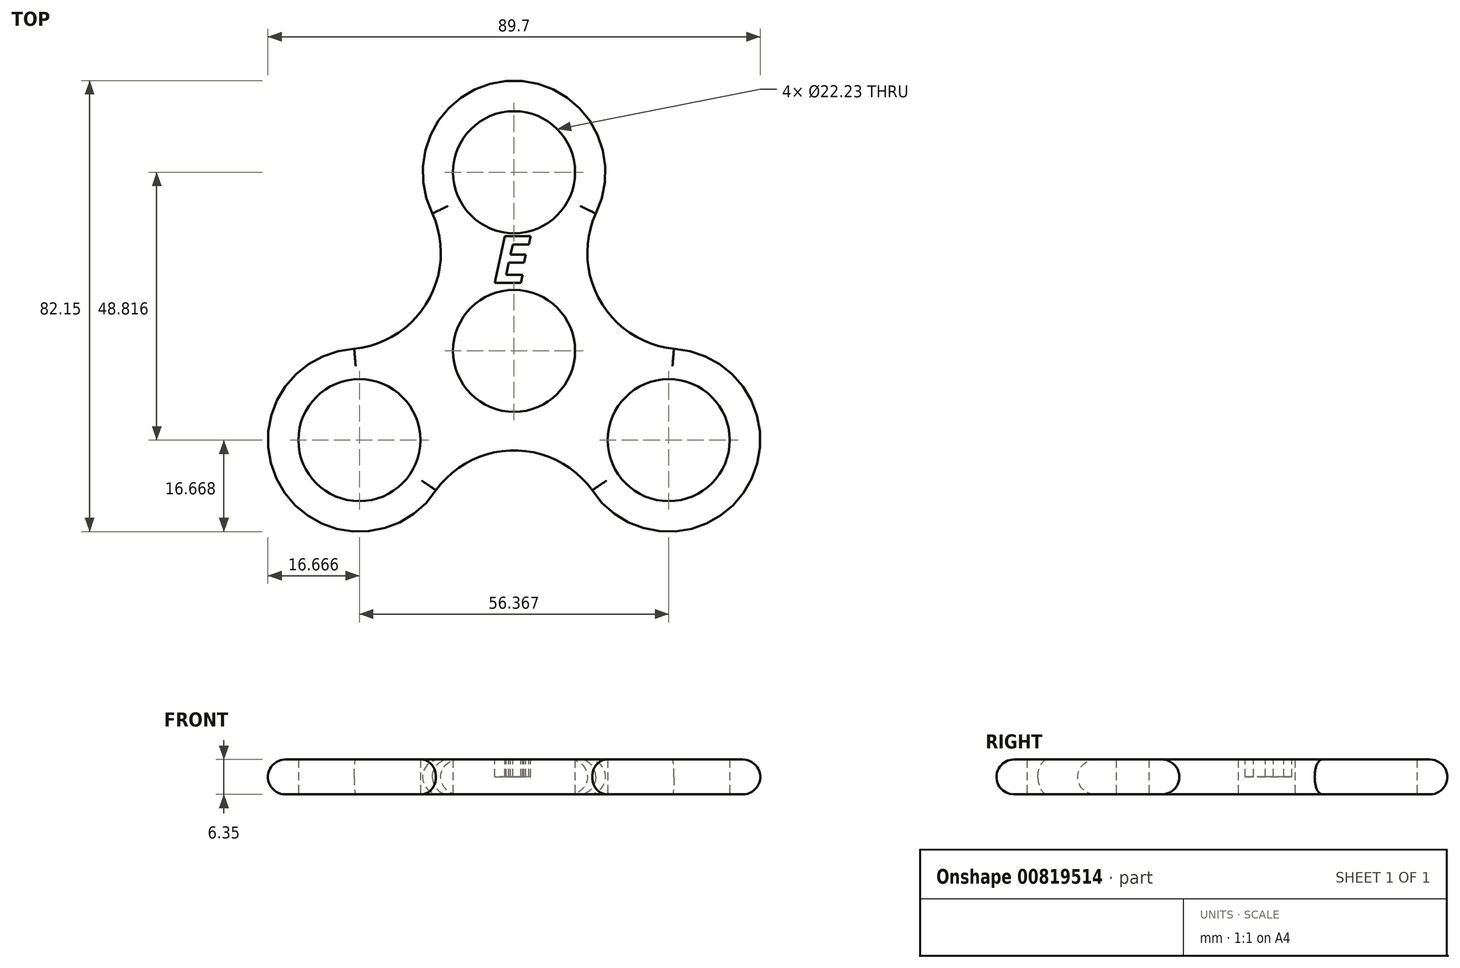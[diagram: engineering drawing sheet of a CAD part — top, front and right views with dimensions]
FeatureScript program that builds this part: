
annotation { "Feature Type Name" : "Feature", "Feature Type Description" : "" }
export const myFeature = defineFeature(function(context is Context, id is Id, definition is map)
    precondition{}
    {
        {
            var Q0;
            Q0=qCreatedBy(makeId("Top.planeOp"),FACE);
            var sketch = newSketch(context, id + "F0", { "sketchPlane" : qUnion([Q0])});
            skCircle(sketch, "E0", {"center": v(0, 0) * mm, "radius": 11.11 * mm});
            skCircle(sketch, "E1", {"center": v(0, 0) * mm, "radius": 15.88 * mm});
            skCircle(sketch, "E2", {"center": v(0, 32.54) * mm, "radius": 16.67 * mm});
            skCircle(sketch, "E3", {"center": v(0, 32.54) * mm, "radius": 11.11 * mm});
            skCircle(sketch, "E4.1.0", {"center": v(-28.18, -16.27) * mm, "radius": 16.67 * mm});
            skCircle(sketch, "E4.1.1", {"center": v(-28.18, -16.27) * mm, "radius": 11.11 * mm});
            skCircle(sketch, "E4.2.0", {"center": v(28.18, -16.27) * mm, "radius": 16.67 * mm});
            skCircle(sketch, "E4.2.1", {"center": v(28.18, -16.27) * mm, "radius": 11.11 * mm});
            skLineSegment(sketch, "E5", {"start": v(0, 0) * mm, "end": v(0, 30.84) * mm, "construction": true});
            skLineSegment(sketch, "E6", {"start": v(0, 0) * mm, "end": v(26.82, 15.49) * mm, "construction": true});
            skLineSegment(sketch, "E7", {"start": v(10.63, 32.4) * mm, "end": v(33.7, -7.55) * mm, "construction": true});
            skArc(sketch, "E8", {"start": v(14.88, 25.03) * mm, "mid": v(15.7, 9.07) * mm, "end": v(29.12, 0.37) * mm});
            skArc(sketch, "E9.1.0", {"start": v(-29.12, 0.37) * mm, "mid": v(-15.7, 9.07) * mm, "end": v(-14.88, 25.03) * mm});
            skArc(sketch, "E9.2.0", {"start": v(14.24, -25.4) * mm, "mid": v(0, -18.14) * mm, "end": v(-14.24, -25.4) * mm});
            skSolve(sketch);
        }
        {
            var Q0;
            Q0=makeQuery(id+"F0.imprint","IMPRINT",FACE,{"disambiguationData":[TD([[makeQuery(id+"F0.imprint","IMPRINT",EDGE,{"derivedFrom":sQuery(id+"F0.wireOp",EDGE,"E3")}),-1.0]])]});
            var Q1;
            {var subQ5=sQuery(id+"F0.wireOp",EDGE,"E9.1.0");Q1=makeQuery(id+"F0.imprint","IMPRINT",FACE,{"disambiguationData":[TD([[makeQuery(id+"F0.imprint","IMPRINT",EDGE,{"derivedFrom":subQ5}),-1.0]])]});}
            var Q2;
            {var subQ5=sQuery(id+"F0.wireOp",EDGE,"E8");Q2=makeQuery(id+"F0.imprint","IMPRINT",FACE,{"disambiguationData":[TD([[makeQuery(id+"F0.imprint","IMPRINT",EDGE,{"derivedFrom":subQ5}),-1.0]])]});}
            var Q3;
            Q3=makeQuery(id+"F0.imprint","IMPRINT",FACE,{"disambiguationData":[TD([[makeQuery(id+"F0.imprint","IMPRINT",EDGE,{"derivedFrom":sQuery(id+"F0.wireOp",EDGE,"E0")}),-1.0]])]});
            var Q4;
            {var subQ5=sQuery(id+"F0.wireOp",EDGE,"E9.2.0");Q4=makeQuery(id+"F0.imprint","IMPRINT",FACE,{"disambiguationData":[TD([[makeQuery(id+"F0.imprint","IMPRINT",EDGE,{"derivedFrom":subQ5}),-1.0]])]});}
            var Q5;
            Q5=makeQuery(id+"F0.imprint","IMPRINT",FACE,{"disambiguationData":[TD([[makeQuery(id+"F0.imprint","IMPRINT",EDGE,{"derivedFrom":sQuery(id+"F0.wireOp",EDGE,"E4.2.1")}),-1.0]])]});
            var Q6;
            Q6=makeQuery(id+"F0.imprint","IMPRINT",FACE,{"disambiguationData":[TD([[makeQuery(id+"F0.imprint","IMPRINT",EDGE,{"derivedFrom":sQuery(id+"F0.wireOp",EDGE,"E4.1.1")}),-1.0]])]});
            extrude(context, id + "F1", {"entities" : qUnion([Q0, Q1, Q2, Q3, Q4, Q5, Q6]), "depth" : 6.35 * mm, "offsetDistance" : 25.4 * mm});
        }
        {
            var Q0;
            Q0=makeQuery(id+"F1.opExtrude","CAP_EDGE",EDGE,{"disambiguationData":[OSD([sQuery(id+"F0.wireOp",EDGE,"E4.1.0")])],"isStart":true});
            var Q1;
            Q1=makeQuery(id+"F1.opExtrude","CAP_EDGE",EDGE,{"disambiguationData":[OSD([sQuery(id+"F0.wireOp",EDGE,"E9.1.0")])],"isStart":true});
            var Q2;
            Q2=makeQuery(id+"F1.opExtrude","CAP_EDGE",EDGE,{"disambiguationData":[OSD([sQuery(id+"F0.wireOp",EDGE,"E9.2.0")])],"isStart":true});
            var Q3;
            Q3=makeQuery(id+"F1.opExtrude","CAP_EDGE",EDGE,{"disambiguationData":[OSD([sQuery(id+"F0.wireOp",EDGE,"E4.2.0")])],"isStart":true});
            var Q4;
            Q4=makeQuery(id+"F1.opExtrude","CAP_EDGE",EDGE,{"disambiguationData":[OSD([sQuery(id+"F0.wireOp",EDGE,"E8")])],"isStart":true});
            var Q5;
            Q5=makeQuery(id+"F1.opExtrude","CAP_EDGE",EDGE,{"disambiguationData":[OSD([sQuery(id+"F0.wireOp",EDGE,"E2")])],"isStart":true});
            var Q6;
            Q6=makeQuery(id+"F1.opExtrude","CAP_EDGE",EDGE,{"disambiguationData":[OSD([sQuery(id+"F0.wireOp",EDGE,"E2")])],"isStart":false});
            var Q7;
            Q7=makeQuery(id+"F1.opExtrude","CAP_EDGE",EDGE,{"disambiguationData":[OSD([sQuery(id+"F0.wireOp",EDGE,"E8")])],"isStart":false});
            var Q8;
            Q8=makeQuery(id+"F1.opExtrude","CAP_EDGE",EDGE,{"disambiguationData":[OSD([sQuery(id+"F0.wireOp",EDGE,"E4.2.0")])],"isStart":false});
            var Q9;
            Q9=makeQuery(id+"F1.opExtrude","CAP_EDGE",EDGE,{"disambiguationData":[OSD([sQuery(id+"F0.wireOp",EDGE,"E9.2.0")])],"isStart":false});
            var Q10;
            Q10=makeQuery(id+"F1.opExtrude","CAP_EDGE",EDGE,{"disambiguationData":[OSD([sQuery(id+"F0.wireOp",EDGE,"E4.1.0")])],"isStart":false});
            var Q11;
            Q11=makeQuery(id+"F1.opExtrude","CAP_EDGE",EDGE,{"disambiguationData":[OSD([sQuery(id+"F0.wireOp",EDGE,"E9.1.0")])],"isStart":false});
            fillet(context, id + "F2", {"entities" : qUnion([Q0, Q1, Q2, Q3, Q4, Q5, Q6, Q7, Q8, Q9, Q10, Q11]), "radius" : 3.17 * mm, "tangentPropagation" : true, "allowEdgeOverflow" : false});
        }
        {
            var Q0;
            Q0=makeQuery(id+"F1.opExtrude","CAP_FACE",FACE,{"disambiguationData":[OSD([sQuery(id+"F0.wireOp",EDGE,"E0"),sQuery(id+"F0.wireOp",EDGE,"E2"),sQuery(id+"F0.wireOp",EDGE,"E3"),sQuery(id+"F0.wireOp",EDGE,"E4.1.0"),sQuery(id+"F0.wireOp",EDGE,"E4.1.1"),sQuery(id+"F0.wireOp",EDGE,"E4.2.0"),sQuery(id+"F0.wireOp",EDGE,"E4.2.1"),sQuery(id+"F0.wireOp",EDGE,"E8"),sQuery(id+"F0.wireOp",EDGE,"E9.1.0"),sQuery(id+"F0.wireOp",EDGE,"E9.2.0")])],"isStart":false});
            var sketch = newSketch(context, id + "F3", { "sketchPlane" : qUnion([Q0])});
            skText(sketch, "E10", { "text": "E", "fontName": "OpenSans-BoldItalic.ttf"});
            const initialGuessF3  = {"E10": [-0.00381, 0.01238, 1, 0, 0.00856]};
            skSetInitialGuess(sketch, initialGuessF3);
            skSolve(sketch);
        }
        {
            var Q0;
            Q0 = qSketchRegion(id + "F3", true);
            extrude(context, id + "F4", {"entities" : qUnion([Q0]), "operationType" : NewBodyOperationType.REMOVE, "oppositeDirection" : true, "depth" : 3.17 * mm, "offsetDistance" : 25.4 * mm});
        }
    });
